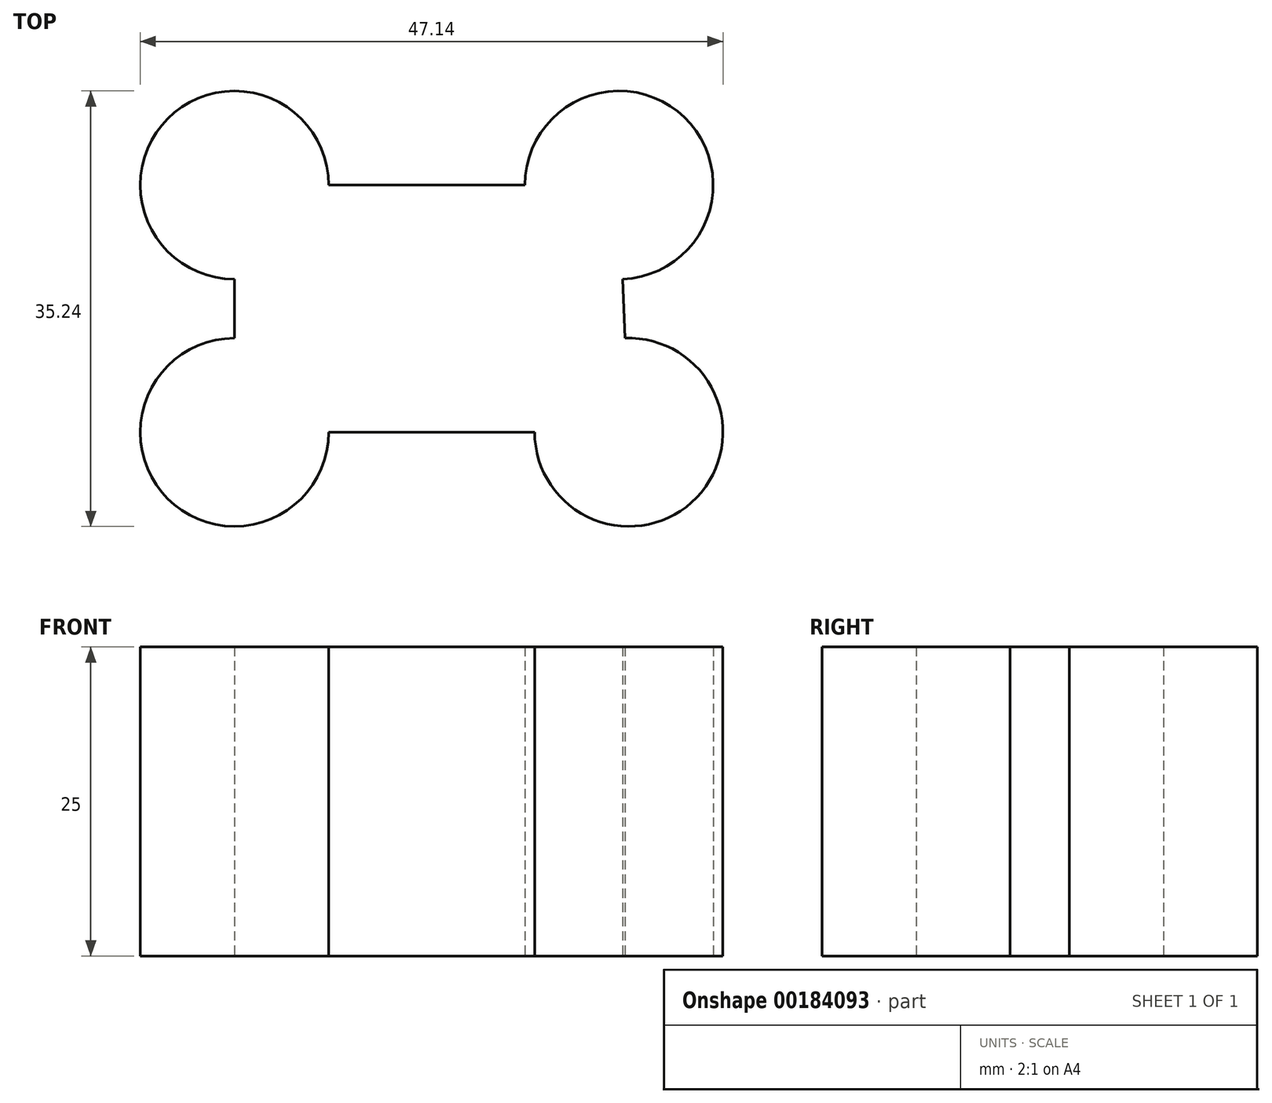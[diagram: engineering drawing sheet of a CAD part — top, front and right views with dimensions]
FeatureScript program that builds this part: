
annotation { "Feature Type Name" : "Feature", "Feature Type Description" : "" }
export const myFeature = defineFeature(function(context is Context, id is Id, definition is map)
    precondition{}
    {
        {
            var Q0;
            Q0=qCreatedBy(makeId("Top.planeOp"),FACE);
            var sketch = newSketch(context, id + "F0", { "sketchPlane" : qUnion([Q0])});
            skLineSegment(sketch, "E0.bottom", {"start": v(0, 20) * mm, "end": v(31.1, 20) * mm});
            skLineSegment(sketch, "E0.top", {"start": v(0, 0) * mm, "end": v(31.9, 0) * mm});
            skLineSegment(sketch, "E0.left", {"start": v(0, 20) * mm, "end": v(0, 0) * mm});
            skLineSegment(sketch, "E0.right", {"start": v(31.11, 20) * mm, "end": v(31.9, 0) * mm});
            skPoint(sketch, "E0.middle", {"position": v(0, 0) * mm});
            skCircle(sketch, "E1", {"center": v(0, 0) * mm, "radius": 7.62 * mm});
            skCircle(sketch, "E2", {"center": v(31.9, 0) * mm, "radius": 7.62 * mm});
            skCircle(sketch, "E3", {"center": v(0, 20) * mm, "radius": 7.62 * mm});
            skCircle(sketch, "E4", {"center": v(31.1, 20) * mm, "radius": 7.62 * mm});
            skSolve(sketch);
        }
        {
            var Q0;
            Q0 = qSketchRegion(id + "F0", true);
            extrude(context, id + "F1", {"entities" : qUnion([Q0]), "depth" : 25 * mm, "offsetDistance" : 25 * mm});
        }
    });
